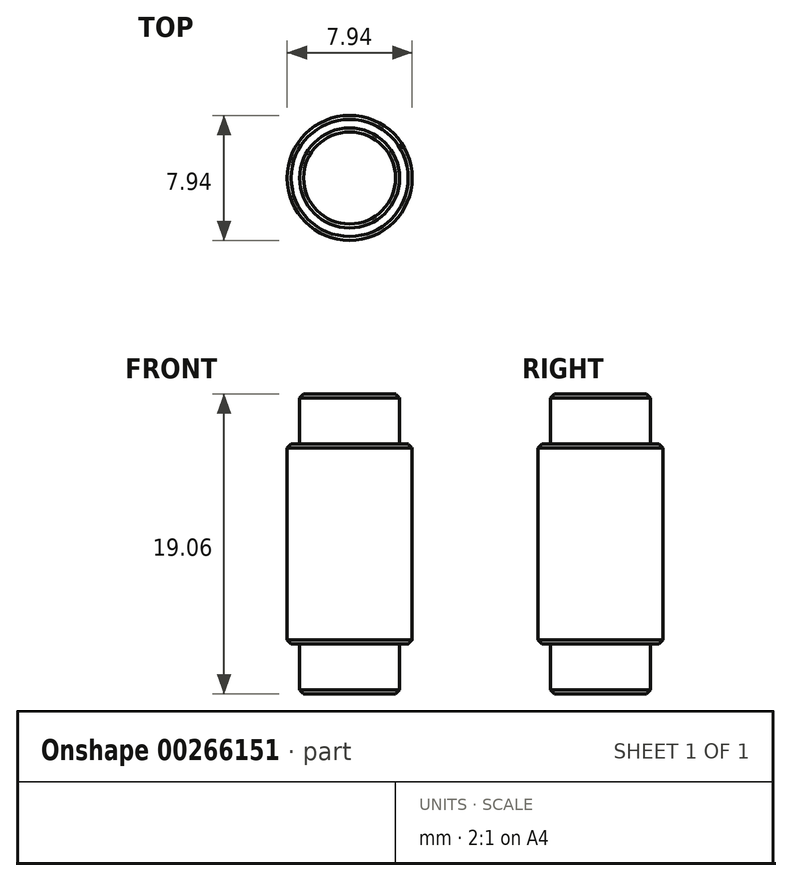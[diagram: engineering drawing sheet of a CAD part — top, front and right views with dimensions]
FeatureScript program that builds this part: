
annotation { "Feature Type Name" : "Feature", "Feature Type Description" : "" }
export const myFeature = defineFeature(function(context is Context, id is Id, definition is map)
    precondition{}
    {
        {
            var Q0;
            Q0=qCreatedBy(makeId("Top.planeOp"),FACE);
            var sketch = newSketch(context, id + "F0", { "sketchPlane" : qUnion([Q0])});
            skCircle(sketch, "E0", {"center": v(0, 0) * mm, "radius": 3.97 * mm});
            skSolve(sketch);
        }
        {
            var Q0;
            Q0=makeQuery(id+"F0.imprint","IMPRINT",FACE,{"disambiguationData":[TD([[makeQuery(id+"F0.imprint","IMPRINT",EDGE,{"derivedFrom":sQuery(id+"F0.wireOp",EDGE,"E0")}),1.0]])]});
            extrude(context, id + "F1", {"entities" : qUnion([Q0]), "depth" : 12.7 * mm});
        }
        {
            var Q0;
            Q0=makeQuery(id+"F1.opExtrude","CAP_FACE",FACE,{"disambiguationData":[OSD([sQuery(id+"F0.wireOp",EDGE,"E0")])],"isStart":false});
            var sketch = newSketch(context, id + "F2", { "sketchPlane" : qUnion([Q0])});
            skCircle(sketch, "E1", {"center": v(0, 0) * mm, "radius": 3.18 * mm});
            skSolve(sketch);
        }
        {
            var Q0;
            Q0=makeQuery(id+"F1.opExtrude","CAP_FACE",FACE,{"disambiguationData":[OSD([sQuery(id+"F0.wireOp",EDGE,"E0")])],"isStart":true});
            var sketch = newSketch(context, id + "F3", { "sketchPlane" : qUnion([Q0])});
            skCircle(sketch, "E2", {"center": v(0, 0) * mm, "radius": 3.18 * mm});
            skSolve(sketch);
        }
        {
            var Q0;
            Q0=makeQuery(id+"F3.imprint","IMPRINT",FACE,{"disambiguationData":[TD([[makeQuery(id+"F3.imprint","IMPRINT",EDGE,{"derivedFrom":sQuery(id+"F3.wireOp",EDGE,"E2")}),1.0]])]});
            extrude(context, id + "F4", {"entities" : qUnion([Q0]), "operationType" : NewBodyOperationType.ADD, "depth" : 3.17 * mm});
        }
        {
            var Q0;
            Q0=makeQuery(id+"F2.imprint","IMPRINT",FACE,{"disambiguationData":[TD([[makeQuery(id+"F2.imprint","IMPRINT",EDGE,{"derivedFrom":sQuery(id+"F2.wireOp",EDGE,"E1")}),1.0]])]});
            extrude(context, id + "F5", {"entities" : qUnion([Q0]), "operationType" : NewBodyOperationType.ADD, "depth" : 3.17 * mm});
        }
        {
            var Q0;
            Q0=makeQuery(id+"F1.opExtrude","CAP_EDGE",EDGE,{"disambiguationData":[OSD([sQuery(id+"F0.wireOp",EDGE,"E0")])],"isStart":false});
            var Q1;
            Q1=makeQuery(id+"F5.opExtrude","CAP_EDGE",EDGE,{"disambiguationData":[OSD([sQuery(id+"F2.wireOp",EDGE,"E1")])],"isStart":false});
            var Q2;
            Q2=makeQuery(id+"F1.opExtrude","CAP_EDGE",EDGE,{"disambiguationData":[OSD([sQuery(id+"F0.wireOp",EDGE,"E0")])],"isStart":true});
            var Q3;
            Q3=makeQuery(id+"F4.opExtrude","CAP_EDGE",EDGE,{"disambiguationData":[OSD([sQuery(id+"F3.wireOp",EDGE,"E2")])],"isStart":false});
            chamfer(context, id + "F6", {"entities" : qUnion([Q0, Q1, Q2, Q3]), "width" : 0.25 * mm, "tangentPropagation" : true});
        }
    });
